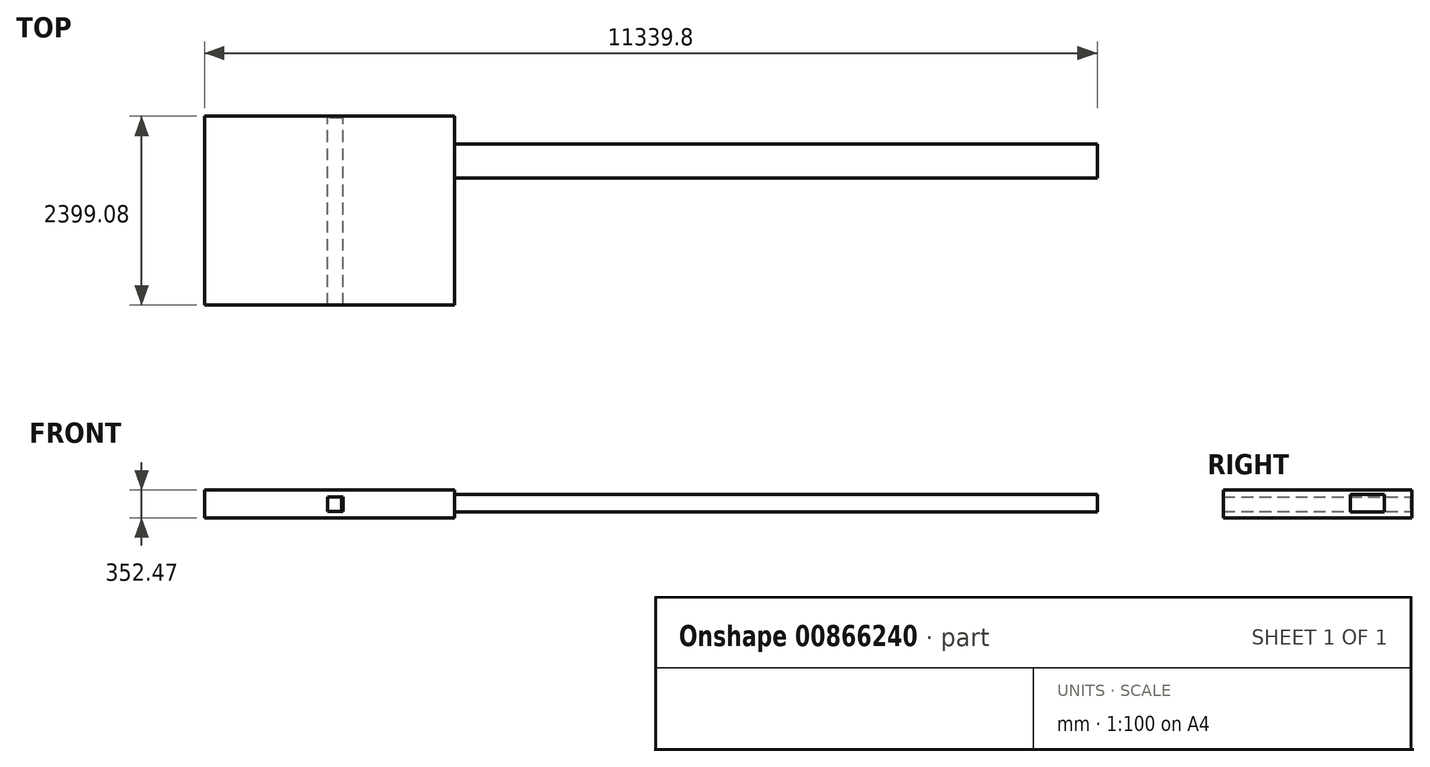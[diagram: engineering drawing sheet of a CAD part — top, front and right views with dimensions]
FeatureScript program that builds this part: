
annotation { "Feature Type Name" : "Feature", "Feature Type Description" : "" }
export const myFeature = defineFeature(function(context is Context, id is Id, definition is map)
    precondition{}
    {
        {
            var Q0;
            Q0=qCreatedBy(makeId("Front.planeOp"),FACE);
            var sketch = newSketch(context, id + "F0", { "sketchPlane" : qUnion([Q0])});
            skLineSegment(sketch, "E0.bottom", {"start": v(101.96, 95.48) * mm, "end": v(-94.78, 95.48) * mm});
            skLineSegment(sketch, "E0.top", {"start": v(101.96, -93.41) * mm, "end": v(-94.78, -93.41) * mm});
            skLineSegment(sketch, "E0.left", {"start": v(101.96, 95.48) * mm, "end": v(101.96, -93.41) * mm});
            skLineSegment(sketch, "E0.right", {"start": v(-94.78, 95.48) * mm, "end": v(-94.78, -93.41) * mm});
            skLineSegment(sketch, "E1.bottom", {"start": v(-1656.3, 180.67) * mm, "end": v(1521.92, 180.67) * mm});
            skLineSegment(sketch, "E1.top", {"start": v(-1656.3, -171.8) * mm, "end": v(1521.92, -171.8) * mm});
            skLineSegment(sketch, "E1.left", {"start": v(-1656.3, 180.67) * mm, "end": v(-1656.3, -171.8) * mm});
            skLineSegment(sketch, "E1.right", {"start": v(1521.92, 180.67) * mm, "end": v(1521.92, -171.8) * mm});
            skSolve(sketch);
        }
        {
            var Q0;
            Q0 = qSketchRegion(id + "F0", true);
            extrude(context, id + "F1", {"entities" : qUnion([Q0]), "depth" : 2399.08 * mm, "offsetDistance" : 25.4 * mm});
        }
        {
            var Q0;
            Q0=qCreatedBy(makeId("Front.planeOp"),FACE);
            var sketch = newSketch(context, id + "F2", { "sketchPlane" : qUnion([Q0])});
            skLineSegment(sketch, "E2.bottom", {"start": v(84, -147.8) * mm, "end": v(-218.76, -147.8) * mm});
            skLineSegment(sketch, "E2.top", {"start": v(84, 154.2) * mm, "end": v(-218.76, 154.2) * mm});
            skLineSegment(sketch, "E2.left", {"start": v(84, -147.8) * mm, "end": v(84, 154.2) * mm});
            skLineSegment(sketch, "E2.right", {"start": v(-218.76, -147.8) * mm, "end": v(-218.76, 154.2) * mm});
            skSolve(sketch);
        }
        {
            var Q0;
            Q0 = qSketchRegion(id + "F2", true);
            extrude(context, id + "F3", {"entities" : qUnion([Q0]), "operationType" : NewBodyOperationType.ADD, "depth" : 25.4 * mm, "offsetDistance" : 25.4 * mm});
        }
        {
            var Q0;
            Q0=makeQuery(id+"F1.opExtrude","SWEPT_FACE",FACE,{"disambiguationData":[OSD([sQuery(id+"F0.wireOp",EDGE,"E1.right")])]});
            var sketch = newSketch(context, id + "F4", { "sketchPlane" : qUnion([Q0])});
            skLineSegment(sketch, "E3.bottom", {"start": v(-786.62, -96.8) * mm, "end": v(-355.22, -96.8) * mm});
            skLineSegment(sketch, "E3.top", {"start": v(-786.62, 121.93) * mm, "end": v(-355.22, 121.93) * mm});
            skLineSegment(sketch, "E3.left", {"start": v(-786.62, -96.8) * mm, "end": v(-786.62, 121.93) * mm});
            skLineSegment(sketch, "E3.right", {"start": v(-355.22, -96.8) * mm, "end": v(-355.22, 121.93) * mm});
            skSolve(sketch);
        }
        {
            var Q0;
            Q0 = qSketchRegion(id + "F4", true);
            extrude(context, id + "F5", {"entities" : qUnion([Q0]), "operationType" : NewBodyOperationType.ADD, "depth" : 25.4 * mm, "offsetDistance" : 25.4 * mm});
        }
        {
            var Q0;
            Q0=makeQuery(id+"F5.opExtrude","CAP_FACE",FACE,{"disambiguationData":[OSD([sQuery(id+"F4.wireOp",EDGE,"E3.bottom"),sQuery(id+"F4.wireOp",EDGE,"E3.top"),sQuery(id+"F4.wireOp",EDGE,"E3.left"),sQuery(id+"F4.wireOp",EDGE,"E3.right")])],"isStart":false});
            var sketch = newSketch(context, id + "F6", { "sketchPlane" : qUnion([Q0])});
            skLineSegment(sketch, "E4.bottom", {"start": v(-786.62, -96.8) * mm, "end": v(-355.22, -96.8) * mm});
            skLineSegment(sketch, "E4.top", {"start": v(-786.62, 121.93) * mm, "end": v(-355.22, 121.93) * mm});
            skLineSegment(sketch, "E4.left", {"start": v(-786.62, -96.8) * mm, "end": v(-786.62, 121.93) * mm});
            skLineSegment(sketch, "E4.right", {"start": v(-355.22, -96.8) * mm, "end": v(-355.22, 121.93) * mm});
            skSolve(sketch);
        }
        {
            var Q0;
            Q0 = qSketchRegion(id + "F6", true);
            extrude(context, id + "F7", {"entities" : qUnion([Q0]), "operationType" : NewBodyOperationType.ADD, "depth" : 8136.21 * mm, "offsetDistance" : 25.4 * mm});
        }
    });
